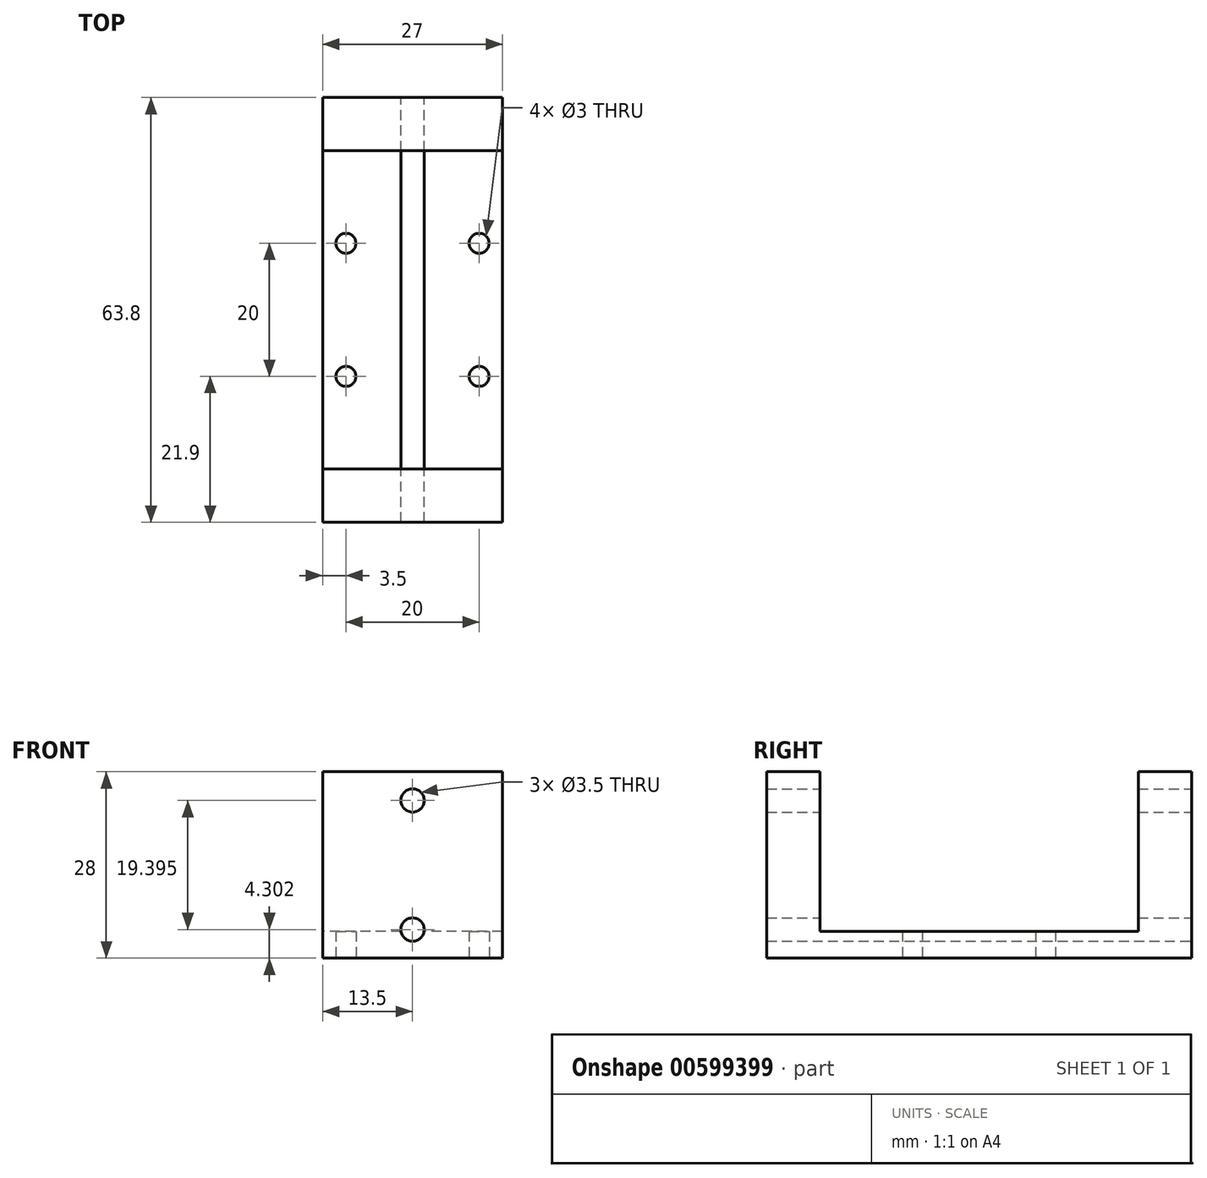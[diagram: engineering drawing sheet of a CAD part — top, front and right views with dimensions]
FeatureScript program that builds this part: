
annotation { "Feature Type Name" : "Feature", "Feature Type Description" : "" }
export const myFeature = defineFeature(function(context is Context, id is Id, definition is map)
    precondition{}
    {
        {
            var Q0;
            Q0=qCreatedBy(makeId("Top.planeOp"),FACE);
            var sketch = newSketch(context, id + "F0", { "sketchPlane" : qUnion([Q0])});
            skLineSegment(sketch, "E0.bottom", {"start": v(-13.5, 21.9) * mm, "end": v(13.5, 21.9) * mm, "construction": true});
            skLineSegment(sketch, "E0.top", {"start": v(-13.5, -21.9) * mm, "end": v(13.5, -21.9) * mm, "construction": true});
            skLineSegment(sketch, "E0.left", {"start": v(-13.5, 21.9) * mm, "end": v(-13.5, -21.9) * mm, "construction": true});
            skLineSegment(sketch, "E0.right", {"start": v(13.5, 21.9) * mm, "end": v(13.5, -21.9) * mm, "construction": true});
            skCircle(sketch, "E1", {"center": v(-10, 10) * mm, "radius": 1.5 * mm, "construction": true});
            skCircle(sketch, "E2", {"center": v(10, 10) * mm, "radius": 1.5 * mm, "construction": true});
            skCircle(sketch, "E3", {"center": v(10, -10) * mm, "radius": 1.5 * mm, "construction": true});
            skCircle(sketch, "E4", {"center": v(-10, -10) * mm, "radius": 1.5 * mm, "construction": true});
            skSolve(sketch);
        }
        {
            var Q0;
            Q0=qCreatedBy(makeId("Top.planeOp"),FACE);
            var sketch = newSketch(context, id + "F1", { "sketchPlane" : qUnion([Q0])});
            skLineSegment(sketch, "E5.0", {"start": v(-13.5, 21.9) * mm, "end": v(-13.5, -21.9) * mm});
            skLineSegment(sketch, "E6.0", {"start": v(-13.5, 21.9) * mm, "end": v(13.5, 21.9) * mm});
            skLineSegment(sketch, "E7.0", {"start": v(13.5, 21.9) * mm, "end": v(13.5, -21.9) * mm});
            skLineSegment(sketch, "E8.0", {"start": v(-13.5, -21.9) * mm, "end": v(13.5, -21.9) * mm});
            skPoint(sketch, "E9.0", {"position": v(-10, -10) * mm});
            skPoint(sketch, "E10.0", {"position": v(10, -10) * mm});
            skPoint(sketch, "E11.0", {"position": v(10, 10) * mm});
            skCircle(sketch, "E12.0", {"center": v(-10, -10) * mm, "radius": 1.5 * mm});
            skCircle(sketch, "E13.0", {"center": v(10, -10) * mm, "radius": 1.5 * mm});
            skCircle(sketch, "E14.0", {"center": v(10, 10) * mm, "radius": 1.5 * mm});
            skCircle(sketch, "E15.0", {"center": v(-10, 10) * mm, "radius": 1.5 * mm});
            skLineSegment(sketch, "E16.top", {"start": v(-13.5, -31.9) * mm, "end": v(13.5, -31.9) * mm});
            skLineSegment(sketch, "E16.left", {"start": v(-13.5, -21.9) * mm, "end": v(-13.5, -31.9) * mm});
            skLineSegment(sketch, "E16.right", {"start": v(13.5, -21.9) * mm, "end": v(13.5, -31.9) * mm});
            skLineSegment(sketch, "E17.top", {"start": v(-13.5, 31.9) * mm, "end": v(13.5, 31.9) * mm});
            skLineSegment(sketch, "E17.left", {"start": v(-13.5, 21.9) * mm, "end": v(-13.5, 31.9) * mm});
            skLineSegment(sketch, "E17.right", {"start": v(13.5, 21.9) * mm, "end": v(13.5, 31.9) * mm});
            skSolve(sketch);
        }
        {
            var Q0;
            Q0=qSketchRegion(id+"F1",true);
            extrude(context, id + "F2", {"entities" : qUnion([Q0]), "depth" : 28 * mm, "offsetDistance" : 25 * mm});
        }
        {
            var Q0;
            Q0=makeQuery(id+"F2.opExtrude","SWEPT_FACE",FACE,{"disambiguationData":[OSD([sQuery(id+"F1.wireOp",EDGE,"E17.top")])]});
            var sketch = newSketch(context, id + "F3", { "sketchPlane" : qUnion([Q0])});
            skPoint(sketch, "E18.centerSnap0", {"position": v(0, 28) * mm});
            skCircle(sketch, "E19", {"center": v(0, 23.7) * mm, "radius": 1.75 * mm});
            skCircle(sketch, "E20", {"center": v(0, 4.3) * mm, "radius": 1.75 * mm});
            skSolve(sketch);
        }
        {
            var Q0;
            Q0=qSketchRegion(id+"F3",true);
            extrude(context, id + "F4", {"entities" : qUnion([Q0]), "operationType" : NewBodyOperationType.REMOVE, "endBound" : BoundingType.THROUGH_ALL, "oppositeDirection" : true, "depth" : 25 * mm, "offsetDistance" : 25 * mm});
        }
        {
            var Q0;
            Q0=makeQuery(id+"F2.opExtrude","SWEPT_FACE",FACE,{"disambiguationData":[OSD([sQuery(id+"F1.wireOp",EDGE,"E5.0"),sQuery(id+"F1.wireOp",EDGE,"E16.left"),sQuery(id+"F1.wireOp",EDGE,"E17.left")])]});
            var sketch = newSketch(context, id + "F5", { "sketchPlane" : qUnion([Q0])});
            skLineSegment(sketch, "E21.bottom", {"start": v(-23.9, 28) * mm, "end": v(23.9, 28) * mm});
            skLineSegment(sketch, "E21.top", {"start": v(-23.9, 4) * mm, "end": v(23.9, 4) * mm});
            skLineSegment(sketch, "E21.left", {"start": v(-23.9, 28) * mm, "end": v(-23.9, 4) * mm});
            skLineSegment(sketch, "E21.right", {"start": v(23.9, 28) * mm, "end": v(23.9, 4) * mm});
            skSolve(sketch);
        }
        {
            var Q0;
            Q0=qSketchRegion(id+"F5",true);
            extrude(context, id + "F6", {"entities" : qUnion([Q0]), "operationType" : NewBodyOperationType.REMOVE, "endBound" : BoundingType.THROUGH_ALL, "oppositeDirection" : true, "depth" : 25 * mm, "offsetDistance" : 25 * mm});
        }
    });
